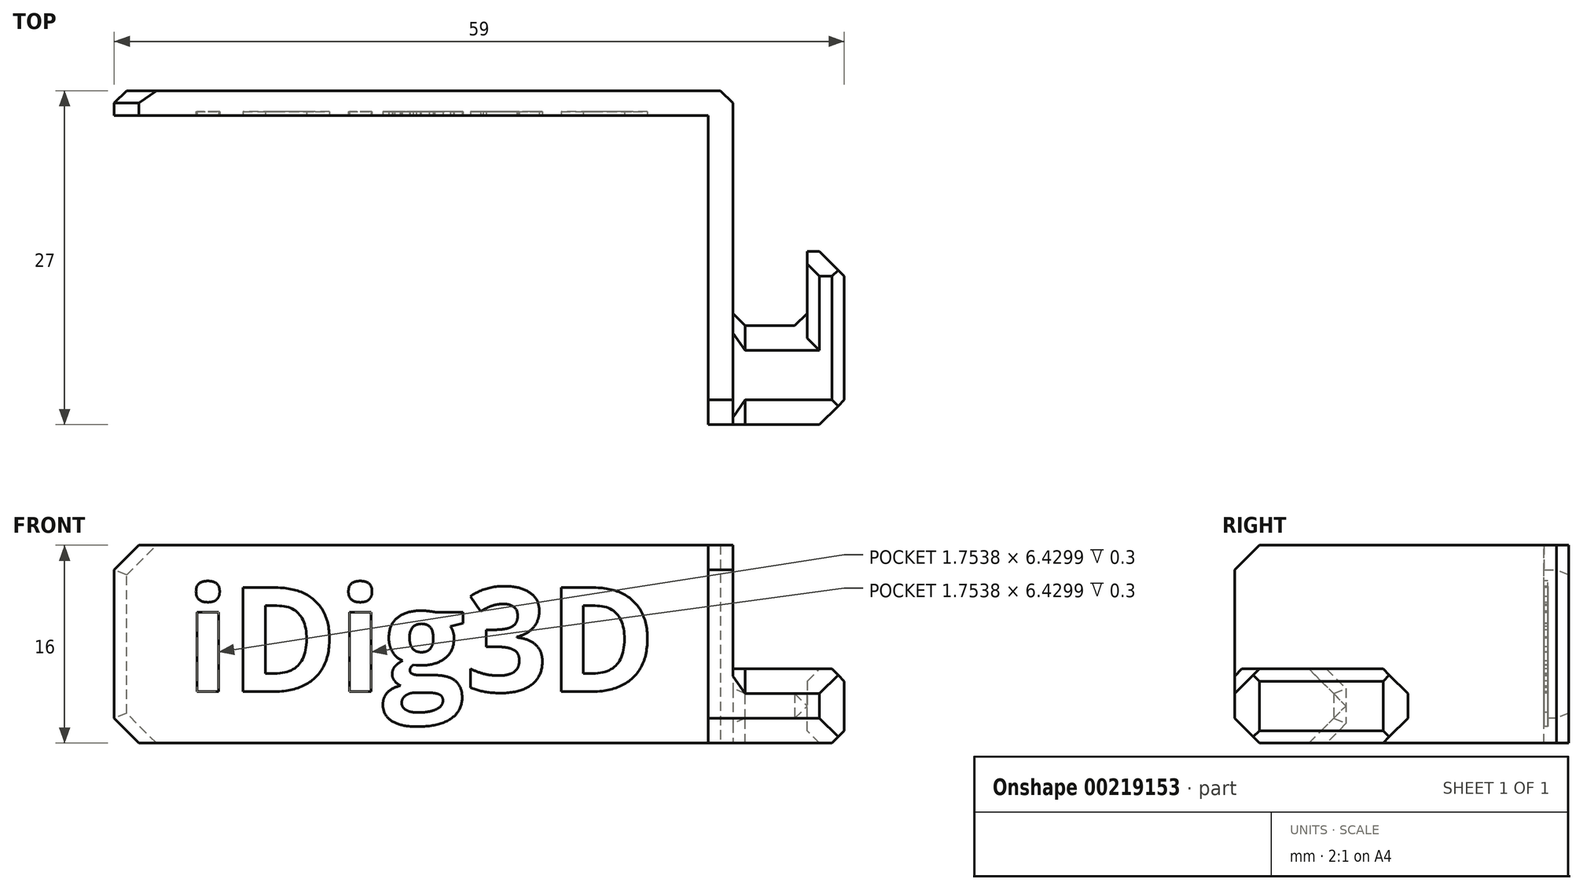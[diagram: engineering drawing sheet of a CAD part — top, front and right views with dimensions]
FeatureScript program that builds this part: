
annotation { "Feature Type Name" : "Feature", "Feature Type Description" : "" }
export const myFeature = defineFeature(function(context is Context, id is Id, definition is map)
    precondition{}
    {
        {
            var Q0;
            Q0=qCreatedBy(makeId("Top.planeOp"),FACE);
            var sketch = newSketch(context, id + "F0", { "sketchPlane" : qUnion([Q0])});
            skLineSegment(sketch, "E0", {"start": v(-50, 0) * mm, "end": v(0, 0) * mm});
            skLineSegment(sketch, "E1", {"start": v(0, 0) * mm, "end": v(0, -19) * mm});
            skLineSegment(sketch, "E2", {"start": v(0, -27) * mm, "end": v(6, -27) * mm});
            skLineSegment(sketch, "E3", {"start": v(6, -19) * mm, "end": v(0, -19) * mm});
            skLineSegment(sketch, "E4", {"start": v(0, -27) * mm, "end": v(-2, -27) * mm});
            skLineSegment(sketch, "E5", {"start": v(-2, -27) * mm, "end": v(-2, -2) * mm});
            skLineSegment(sketch, "E6", {"start": v(-2, -2) * mm, "end": v(-50, -2) * mm});
            skLineSegment(sketch, "E7", {"start": v(-50, -2) * mm, "end": v(-50, 0) * mm});
            skLineSegment(sketch, "E8.bottom", {"start": v(6, -13) * mm, "end": v(9, -13) * mm});
            skLineSegment(sketch, "E8.top", {"start": v(6, -27) * mm, "end": v(9, -27) * mm, "construction": true});
            skLineSegment(sketch, "E8.right", {"start": v(9, -13) * mm, "end": v(9, -27) * mm});
            skLineSegment(sketch, "E9", {"start": v(6, -19) * mm, "end": v(6, -13) * mm});
            skPoint(sketch, "E10.visualSharp", {"position": v(-2, -27) * mm});
            skLineSegment(sketch, "E11", {"start": v(-2, -2) * mm, "end": v(0, -2) * mm, "construction": true});
            skLineSegment(sketch, "E12", {"start": v(0, -19) * mm, "end": v(0, -27) * mm});
            skLineSegment(sketch, "E13", {"start": v(6, -27) * mm, "end": v(9, -27) * mm});
            skSolve(sketch);
        }
        {
            var Q0;
            Q0 = qSketchRegion(id + "F0", true);
            extrude(context, id + "F1", {"entities" : qUnion([Q0]), "oppositeDirection" : true, "depth" : 6 * mm});
        }
        {
            var Q0;
            Q0=makeQuery(id+"F0.imprint","IMPRINT",FACE,{"disambiguationData":[TD([[makeQuery(id+"F0.imprint","IMPRINT",EDGE,{"derivedFrom":sQuery(id+"F0.wireOp",EDGE,"E0")}),-1.0]])]});
            extrude(context, id + "F2", {"entities" : qUnion([Q0]), "operationType" : NewBodyOperationType.ADD, "depth" : 10 * mm});
        }
        {
            var Q0;
            Q0=makeQuery(id+"F1.opExtrude","CAP_EDGE",EDGE,{"disambiguationData":[OSD([sQuery(id+"F0.wireOp",EDGE,"E3")])],"isStart":false});
            var Q1;
            Q1=makeQuery(id+"F1.opExtrude","CAP_EDGE",EDGE,{"disambiguationData":[OSD([sQuery(id+"F0.wireOp",EDGE,"E2"),sQuery(id+"F0.wireOp",EDGE,"E4")])],"isStart":false});
            var Q2;
            Q2=makeQuery(id+"F1.opExtrude","CAP_EDGE",EDGE,{"disambiguationData":[OSD([sQuery(id+"F0.wireOp",EDGE,"E3")])],"isStart":true});
            var Q3;
            Q3=makeQuery(id+"F1.opExtrude","CAP_EDGE",EDGE,{"disambiguationData":[OSD([sQuery(id+"F0.wireOp",EDGE,"E2"),sQuery(id+"F0.wireOp",EDGE,"E4")])],"isStart":true});
            var Q4;
            Q4=makeQuery(id+"F2.opExtrude","CAP_EDGE",EDGE,{"disambiguationData":[OSD([sQuery(id+"F0.wireOp",EDGE,"E4")])],"isStart":false});
            var Q5;
            Q5=makeQuery(id+"F1.opExtrude","CAP_EDGE",EDGE,{"disambiguationData":[OSD([sQuery(id+"F0.wireOp",EDGE,"E7")])],"isStart":false});
            var Q6;
            Q6=makeQuery(id+"F2.opExtrude","CAP_EDGE",EDGE,{"disambiguationData":[OSD([sQuery(id+"F0.wireOp",EDGE,"E7")])],"isStart":false});
            var Q7;
            Q7=makeQuery(id+"F1.opExtrude","SWEPT_EDGE",EDGE,{"disambiguationData":[OSD([sQuery(id+"F0.wireOp",EDGE,"E8.right"),sQuery(id+"F0.wireOp",EDGE,"E13")])]});
            var Q8;
            Q8=makeQuery(id+"F1.opExtrude","CAP_EDGE",EDGE,{"disambiguationData":[OSD([sQuery(id+"F0.wireOp",EDGE,"E8.bottom")])],"isStart":false});
            var Q9;
            Q9=makeQuery(id+"F1.opExtrude","CAP_EDGE",EDGE,{"disambiguationData":[OSD([sQuery(id+"F0.wireOp",EDGE,"E8.bottom")])],"isStart":true});
            var Q10;
            Q10=makeQuery(id+"F1.opExtrude","SWEPT_EDGE",EDGE,{"disambiguationData":[OSD([sQuery(id+"F0.wireOp",EDGE,"E8.bottom"),sQuery(id+"F0.wireOp",EDGE,"E8.right")])]});
            chamfer(context, id + "F3", {"entities" : qUnion([Q0, Q1, Q2, Q3, Q4, Q5, Q6, Q7, Q8, Q9, Q10]), "width" : 2 * mm, "tangentPropagation" : true});
        }
        {
            var Q0;
            {var subQ0=sQuery(id+"F0.wireOp",EDGE,"E1");Q0=makeQuery(id+"F3.opChamfer","BLEND_EDGE",EDGE,{"blendedFrom":[makeQuery(id+"F1.opExtrude","CAP_EDGE",EDGE,{"disambiguationData":[OSD([sQuery(id+"F0.wireOp",EDGE,"E2"),sQuery(id+"F0.wireOp",EDGE,"E4")])],"isStart":true}),makeQuery(id+"F2.boolean.opBoolean","MERGE",FACE,{"derivedFrom":[makeQuery(id+"F1.opExtrude","SWEPT_FACE",FACE,{"disambiguationData":[OSD([subQ0])]}),makeQuery(id+"F2.opExtrude","SWEPT_FACE",FACE,{"disambiguationData":[OSD([subQ0,sQuery(id+"F0.wireOp",EDGE,"E12")])]})]})],"blendedInto":[makeQuery(id+"F2.boolean.opBoolean","MERGE",FACE,{"derivedFrom":[makeQuery(id+"F1.opExtrude","SWEPT_FACE",FACE,{"disambiguationData":[OSD([subQ0])]}),makeQuery(id+"F2.opExtrude","SWEPT_FACE",FACE,{"disambiguationData":[OSD([subQ0,sQuery(id+"F0.wireOp",EDGE,"E12")])]})]})]});}
            var Q1;
            Q1=makeQuery(id+"F2.opExtrude","CAP_EDGE",EDGE,{"disambiguationData":[OSD([sQuery(id+"F0.wireOp",EDGE,"E1"),sQuery(id+"F0.wireOp",EDGE,"E12")])],"isStart":true});
            var Q2;
            {var subQ0=sQuery(id+"F0.wireOp",EDGE,"E1");Q2=makeQuery(id+"F3.opChamfer","BLEND_EDGE",EDGE,{"blendedFrom":[makeQuery(id+"F1.opExtrude","CAP_EDGE",EDGE,{"disambiguationData":[OSD([sQuery(id+"F0.wireOp",EDGE,"E3")])],"isStart":true}),makeQuery(id+"F2.boolean.opBoolean","MERGE",FACE,{"derivedFrom":[makeQuery(id+"F1.opExtrude","SWEPT_FACE",FACE,{"disambiguationData":[OSD([subQ0])]}),makeQuery(id+"F2.opExtrude","SWEPT_FACE",FACE,{"disambiguationData":[OSD([subQ0,sQuery(id+"F0.wireOp",EDGE,"E12")])]})]})],"blendedInto":[makeQuery(id+"F2.boolean.opBoolean","MERGE",FACE,{"derivedFrom":[makeQuery(id+"F1.opExtrude","SWEPT_FACE",FACE,{"disambiguationData":[OSD([subQ0])]}),makeQuery(id+"F2.opExtrude","SWEPT_FACE",FACE,{"disambiguationData":[OSD([subQ0,sQuery(id+"F0.wireOp",EDGE,"E12")])]})]})]});}
            var Q3;
            Q3=makeQuery(id+"F1.opExtrude","SWEPT_EDGE",EDGE,{"disambiguationData":[OSD([sQuery(id+"F0.wireOp",EDGE,"E1"),sQuery(id+"F0.wireOp",EDGE,"E3"),sQuery(id+"F0.wireOp",EDGE,"E12")])]});
            var Q4;
            Q4=makeQuery(id+"F1.opExtrude","SWEPT_EDGE",EDGE,{"disambiguationData":[OSD([sQuery(id+"F0.wireOp",EDGE,"E3"),sQuery(id+"F0.wireOp",EDGE,"E9")])]});
            var Q5;
            Q5=makeQuery(id+"F3.opChamfer","BLEND_EDGE",EDGE,{"blendedFrom":[makeQuery(id+"F1.opExtrude","CAP_EDGE",EDGE,{"disambiguationData":[OSD([sQuery(id+"F0.wireOp",EDGE,"E2"),sQuery(id+"F0.wireOp",EDGE,"E4")])],"isStart":true}),makeQuery(id+"F1.opExtrude","SWEPT_FACE",FACE,{"disambiguationData":[OSD([sQuery(id+"F0.wireOp",EDGE,"gosW89bK-c3sy-WAHm-q43c-PLJXgfsevG92")])]})],"blendedInto":[makeQuery(id+"F1.opExtrude","SWEPT_FACE",FACE,{"disambiguationData":[OSD([sQuery(id+"F0.wireOp",EDGE,"gosW89bK-c3sy-WAHm-q43c-PLJXgfsevG92")])]})]});
            var Q6;
            Q6=makeQuery(id+"F1.opExtrude","SWEPT_EDGE",EDGE,{"disambiguationData":[OSD([sQuery(id+"F0.wireOp",EDGE,"E2"),sQuery(id+"F0.wireOp",EDGE,"gosW89bK-c3sy-WAHm-q43c-PLJXgfsevG92")])]});
            var Q7;
            Q7=makeQuery(id+"F3.opChamfer","BLEND_EDGE",EDGE,{"blendedFrom":[makeQuery(id+"F1.opExtrude","CAP_EDGE",EDGE,{"disambiguationData":[OSD([sQuery(id+"F0.wireOp",EDGE,"E2"),sQuery(id+"F0.wireOp",EDGE,"E4")])],"isStart":false}),makeQuery(id+"F1.opExtrude","SWEPT_FACE",FACE,{"disambiguationData":[OSD([sQuery(id+"F0.wireOp",EDGE,"gosW89bK-c3sy-WAHm-q43c-PLJXgfsevG92")])]})],"blendedInto":[makeQuery(id+"F1.opExtrude","SWEPT_FACE",FACE,{"disambiguationData":[OSD([sQuery(id+"F0.wireOp",EDGE,"gosW89bK-c3sy-WAHm-q43c-PLJXgfsevG92")])]})]});
            var Q8;
            Q8=makeQuery(id+"F1.opExtrude","CAP_EDGE",EDGE,{"disambiguationData":[OSD([sQuery(id+"F0.wireOp",EDGE,"E8.right")])],"isStart":false});
            var Q9;
            Q9=makeQuery(id+"F1.opExtrude","CAP_EDGE",EDGE,{"disambiguationData":[OSD([sQuery(id+"F0.wireOp",EDGE,"E8.right")])],"isStart":true});
            var Q10;
            {var subQ0=sQuery(id+"F0.wireOp",EDGE,"E7");var subQ1=sQuery(id+"F0.wireOp",EDGE,"E0");Q10=makeQuery(id+"F2.boolean.opBoolean","MERGE",EDGE,{"derivedFrom":[makeQuery(id+"F1.opExtrude","SWEPT_EDGE",EDGE,{"disambiguationData":[OSD([subQ1,subQ0])]}),makeQuery(id+"F2.opExtrude","SWEPT_EDGE",EDGE,{"disambiguationData":[OSD([subQ1,subQ0])]})]});}
            var Q11;
            {var subQ0=sQuery(id+"F0.wireOp",EDGE,"E0");Q11=makeQuery(id+"F3.opChamfer","BLEND_EDGE",EDGE,{"blendedFrom":[makeQuery(id+"F1.opExtrude","CAP_EDGE",EDGE,{"disambiguationData":[OSD([sQuery(id+"F0.wireOp",EDGE,"E7")])],"isStart":false}),makeQuery(id+"F2.boolean.opBoolean","MERGE",FACE,{"derivedFrom":[makeQuery(id+"F1.opExtrude","SWEPT_FACE",FACE,{"disambiguationData":[OSD([subQ0])]}),makeQuery(id+"F2.opExtrude","SWEPT_FACE",FACE,{"disambiguationData":[OSD([subQ0])]})]})],"blendedInto":[makeQuery(id+"F2.boolean.opBoolean","MERGE",FACE,{"derivedFrom":[makeQuery(id+"F1.opExtrude","SWEPT_FACE",FACE,{"disambiguationData":[OSD([subQ0])]}),makeQuery(id+"F2.opExtrude","SWEPT_FACE",FACE,{"disambiguationData":[OSD([subQ0])]})]})]});}
            var Q12;
            {var subQ0=sQuery(id+"F0.wireOp",EDGE,"E0");Q12=makeQuery(id+"F3.opChamfer","BLEND_EDGE",EDGE,{"blendedFrom":[makeQuery(id+"F2.opExtrude","CAP_EDGE",EDGE,{"disambiguationData":[OSD([sQuery(id+"F0.wireOp",EDGE,"E7")])],"isStart":false}),makeQuery(id+"F2.boolean.opBoolean","MERGE",FACE,{"derivedFrom":[makeQuery(id+"F1.opExtrude","SWEPT_FACE",FACE,{"disambiguationData":[OSD([subQ0])]}),makeQuery(id+"F2.opExtrude","SWEPT_FACE",FACE,{"disambiguationData":[OSD([subQ0])]})]})],"blendedInto":[makeQuery(id+"F2.boolean.opBoolean","MERGE",FACE,{"derivedFrom":[makeQuery(id+"F1.opExtrude","SWEPT_FACE",FACE,{"disambiguationData":[OSD([subQ0])]}),makeQuery(id+"F2.opExtrude","SWEPT_FACE",FACE,{"disambiguationData":[OSD([subQ0])]})]})]});}
            var Q13;
            {var subQ0=sQuery(id+"F0.wireOp",EDGE,"E1");var subQ1=sQuery(id+"F0.wireOp",EDGE,"E0");Q13=makeQuery(id+"F2.boolean.opBoolean","MERGE",EDGE,{"derivedFrom":[makeQuery(id+"F1.opExtrude","SWEPT_EDGE",EDGE,{"disambiguationData":[OSD([subQ1,subQ0])]}),makeQuery(id+"F2.opExtrude","SWEPT_EDGE",EDGE,{"disambiguationData":[OSD([subQ1,subQ0])]})]});}
            var Q14;
            Q14=makeQuery(id+"F1.opExtrude","CAP_EDGE",EDGE,{"disambiguationData":[OSD([sQuery(id+"F0.wireOp",EDGE,"usbSmMso-nL9y-jO2h-OWm9-LmaHcrWbFYOW")])],"isStart":false});
            var Q15;
            Q15=makeQuery(id+"F1.opExtrude","CAP_EDGE",EDGE,{"disambiguationData":[OSD([sQuery(id+"F0.wireOp",EDGE,"usbSmMso-nL9y-jO2h-OWm9-LmaHcrWbFYOW")])],"isStart":true});
            var Q16;
            Q16=makeQuery(id+"F1.opExtrude","CAP_EDGE",EDGE,{"disambiguationData":[OSD([sQuery(id+"F0.wireOp",EDGE,"gosW89bK-c3sy-WAHm-q43c-PLJXgfsevG92")])],"isStart":false});
            var Q17;
            Q17=makeQuery(id+"F1.opExtrude","CAP_EDGE",EDGE,{"disambiguationData":[OSD([sQuery(id+"F0.wireOp",EDGE,"gosW89bK-c3sy-WAHm-q43c-PLJXgfsevG92")])],"isStart":true});
            var Q18;
            Q18=makeQuery(id+"F1.opExtrude","CAP_EDGE",EDGE,{"disambiguationData":[OSD([sQuery(id+"F0.wireOp",EDGE,"E9")])],"isStart":true});
            var Q19;
            Q19=makeQuery(id+"F1.opExtrude","CAP_EDGE",EDGE,{"disambiguationData":[OSD([sQuery(id+"F0.wireOp",EDGE,"E9")])],"isStart":false});
            var Q20;
            {var subQ0=sQuery(id+"F0.wireOp",EDGE,"E1");Q20=makeQuery(id+"F3.opChamfer","BLEND_EDGE",EDGE,{"blendedFrom":[makeQuery(id+"F1.opExtrude","CAP_EDGE",EDGE,{"disambiguationData":[OSD([sQuery(id+"F0.wireOp",EDGE,"E3")])],"isStart":false}),makeQuery(id+"F2.boolean.opBoolean","MERGE",FACE,{"derivedFrom":[makeQuery(id+"F1.opExtrude","SWEPT_FACE",FACE,{"disambiguationData":[OSD([subQ0])]}),makeQuery(id+"F2.opExtrude","SWEPT_FACE",FACE,{"disambiguationData":[OSD([subQ0,sQuery(id+"F0.wireOp",EDGE,"E12")])]})]})],"blendedInto":[makeQuery(id+"F2.boolean.opBoolean","MERGE",FACE,{"derivedFrom":[makeQuery(id+"F1.opExtrude","SWEPT_FACE",FACE,{"disambiguationData":[OSD([subQ0])]}),makeQuery(id+"F2.opExtrude","SWEPT_FACE",FACE,{"disambiguationData":[OSD([subQ0,sQuery(id+"F0.wireOp",EDGE,"E12")])]})]})]});}
            chamfer(context, id + "F4", {"entities" : qUnion([Q0, Q1, Q2, Q3, Q4, Q5, Q6, Q7, Q8, Q9, Q10, Q11, Q12, Q13, Q14, Q15, Q16, Q17, Q18, Q19, Q20]), "width" : 1 * mm, "tangentPropagation" : true});
        }
        {
            var Q0;
            {var subQ0=sQuery(id+"F0.wireOp",EDGE,"E6");Q0=makeQuery(id+"F2.boolean.opBoolean","MERGE",FACE,{"derivedFrom":[makeQuery(id+"F1.opExtrude","SWEPT_FACE",FACE,{"disambiguationData":[OSD([subQ0])]}),makeQuery(id+"F2.opExtrude","SWEPT_FACE",FACE,{"disambiguationData":[OSD([subQ0])]})]});}
            var sketch = newSketch(context, id + "F5", { "sketchPlane" : qUnion([Q0])});
            skText(sketch, "E14", { "text": "iDig3D", "fontName": "OpenSans-Bold.ttf"});
            const initialGuessF5  = {"E14": [-0.04423, -0.00184, 1, 0, 0.00848]};
            skSetInitialGuess(sketch, initialGuessF5);
            skSolve(sketch);
        }
        {
            var Q0;
            Q0 = qSketchRegion(id + "F5", true);
            extrude(context, id + "F6", {"entities" : qUnion([Q0]), "operationType" : NewBodyOperationType.REMOVE, "oppositeDirection" : true, "depth" : 0.3 * mm});
        }
    });
